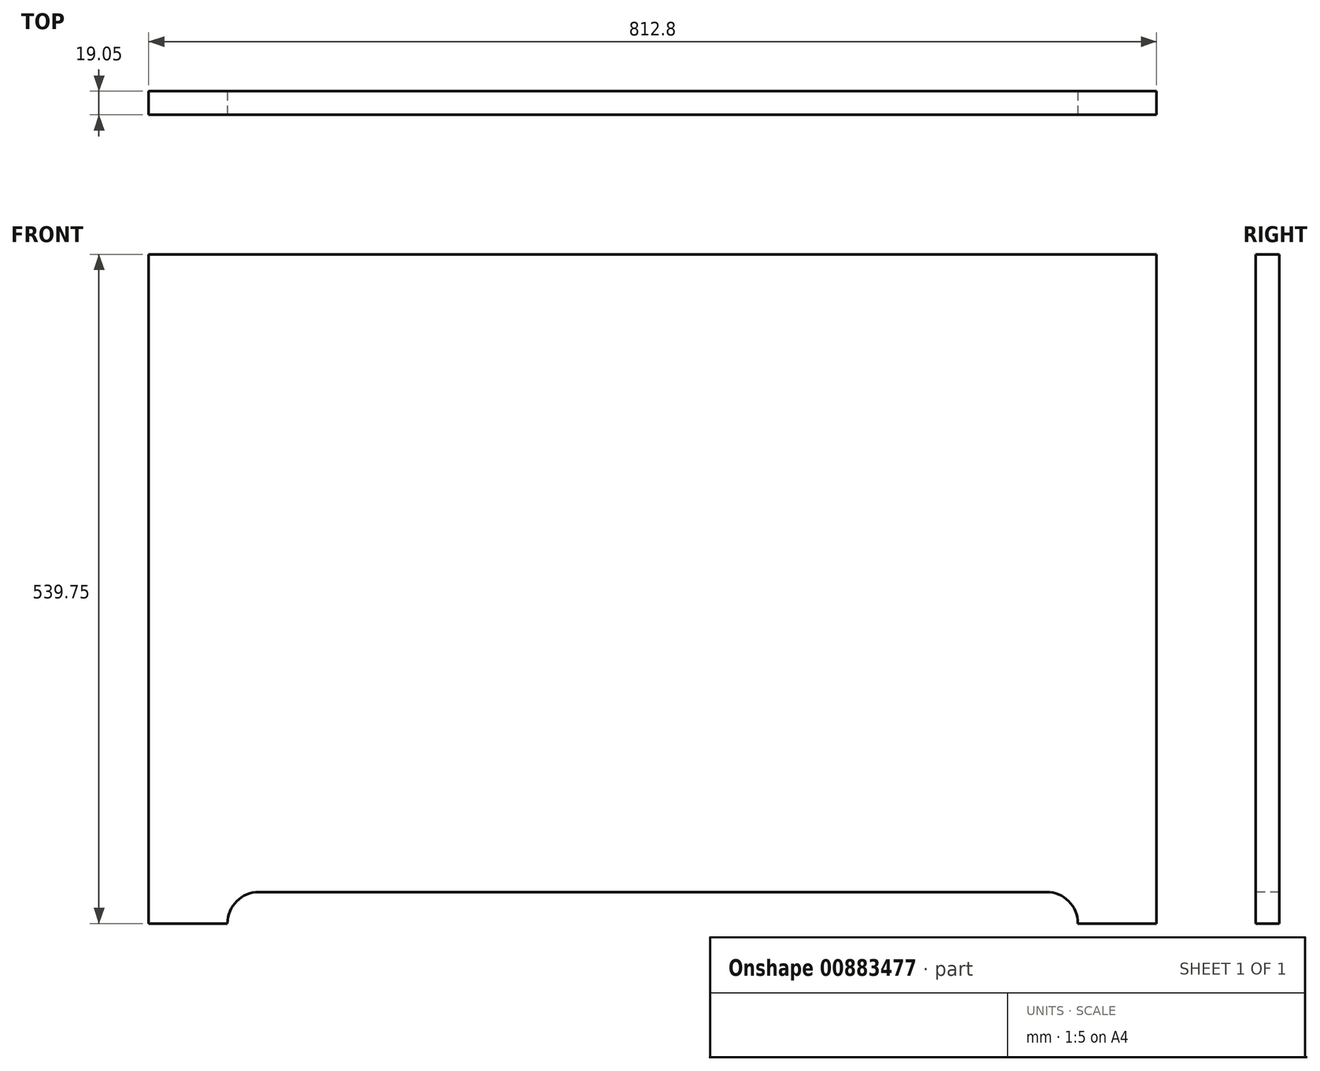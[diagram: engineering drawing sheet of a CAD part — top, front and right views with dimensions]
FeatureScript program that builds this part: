
annotation { "Feature Type Name" : "Feature", "Feature Type Description" : "" }
export const myFeature = defineFeature(function(context is Context, id is Id, definition is map)
    precondition{}
    {
        {
            var Q0;
            Q0=qCreatedBy(makeId("Front.planeOp"),FACE);
            var sketch = newSketch(context, id + "F0", { "sketchPlane" : qUnion([Q0])});
            skLineSegment(sketch, "E0.bottom", {"start": v(0, 0) * mm, "end": v(812.8, 0) * mm});
            skLineSegment(sketch, "E0.top", {"start": v(0, 539.75) * mm, "end": v(812.8, 539.75) * mm});
            skLineSegment(sketch, "E0.left", {"start": v(0, 0) * mm, "end": v(0, 539.75) * mm});
            skLineSegment(sketch, "E0.right", {"start": v(812.8, 0) * mm, "end": v(812.8, 539.75) * mm});
            skSolve(sketch);
        }
        {
            var Q0;
            Q0 = qSketchRegion(id + "F0", true);
            extrude(context, id + "F1", {"entities" : qUnion([Q0]), "depth" : 19.05 * mm, "offsetDistance" : 25.4 * mm});
        }
        {
            var Q0;
            Q0=makeQuery(id+"F1.opExtrude","CAP_FACE",FACE,{"disambiguationData":[OSD([sQuery(id+"F0.wireOp",EDGE,"E0.bottom"),sQuery(id+"F0.wireOp",EDGE,"E0.top"),sQuery(id+"F0.wireOp",EDGE,"E0.left"),sQuery(id+"F0.wireOp",EDGE,"E0.right")])],"isStart":false});
            var sketch = newSketch(context, id + "F2", { "sketchPlane" : qUnion([Q0])});
            skArc(sketch, "E1", {"start": v(88.9, 25.4) * mm, "mid": v(70.94, 17.96) * mm, "end": v(63.5, 0) * mm});
            skLineSegment(sketch, "E2", {"start": v(63.5, 0) * mm, "end": v(63.5, -132.16) * mm, "construction": true});
            skLineSegment(sketch, "E3", {"start": v(406.4, 0) * mm, "end": v(406.4, 419.7) * mm, "construction": true});
            skLineSegment(sketch, "E4", {"start": v(88.9, 25.4) * mm, "end": v(406.4, 25.4) * mm});
            skLineSegment(sketch, "E5.MirrorCS", {"start": v(723.9, 25.4) * mm, "end": v(406.4, 25.4) * mm});
            skArc(sketch, "E6.MirrorCS", {"start": v(723.9, 25.4) * mm, "mid": v(741.86, 17.96) * mm, "end": v(749.3, 0) * mm});
            skLineSegment(sketch, "E7", {"start": v(63.5, 0) * mm, "end": v(749.3, 0) * mm});
            skSolve(sketch);
        }
        {
            var Q0;
            Q0 = qSketchRegion(id + "F2", true);
            extrude(context, id + "F3", {"entities" : qUnion([Q0]), "operationType" : NewBodyOperationType.REMOVE, "oppositeDirection" : true, "depth" : 25.4 * mm, "offsetDistance" : 25.4 * mm});
        }
    });
